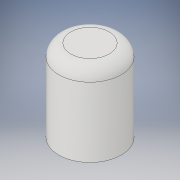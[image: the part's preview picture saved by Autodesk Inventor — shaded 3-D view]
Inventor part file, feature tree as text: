
AUTODESK INVENTOR PART (.ipt)
format: ipt  version: 2018 (Build 220112000, 112)  size: 117,760 bytes
history: native  units: in
note: dims shown in document units (in); Inventor stores cm internally (conversion verified against a paired STEP export)
features: extrude x1, shell x1, fillet x1, sketch x1
ambient origin geometry x8: Origin, YZ Plane, XZ Plane, XY Plane, X Axis, Y Axis, Z Axis, Center Point
bodies: Solid1 (feature_tree)
feature tree (4):
  extrude  "Extrusion1"  Depth=0.425in TaperAngle=0.0deg
  shell  "Shell1"  Thickness=0.025in
  fillet  "Fillet1"  Radius=0.0625in
  sketch  "Sketch1"  dims[d0=0.325in d1=0.425in d2=0.0in d3=0.025in d4=0.0625in]
